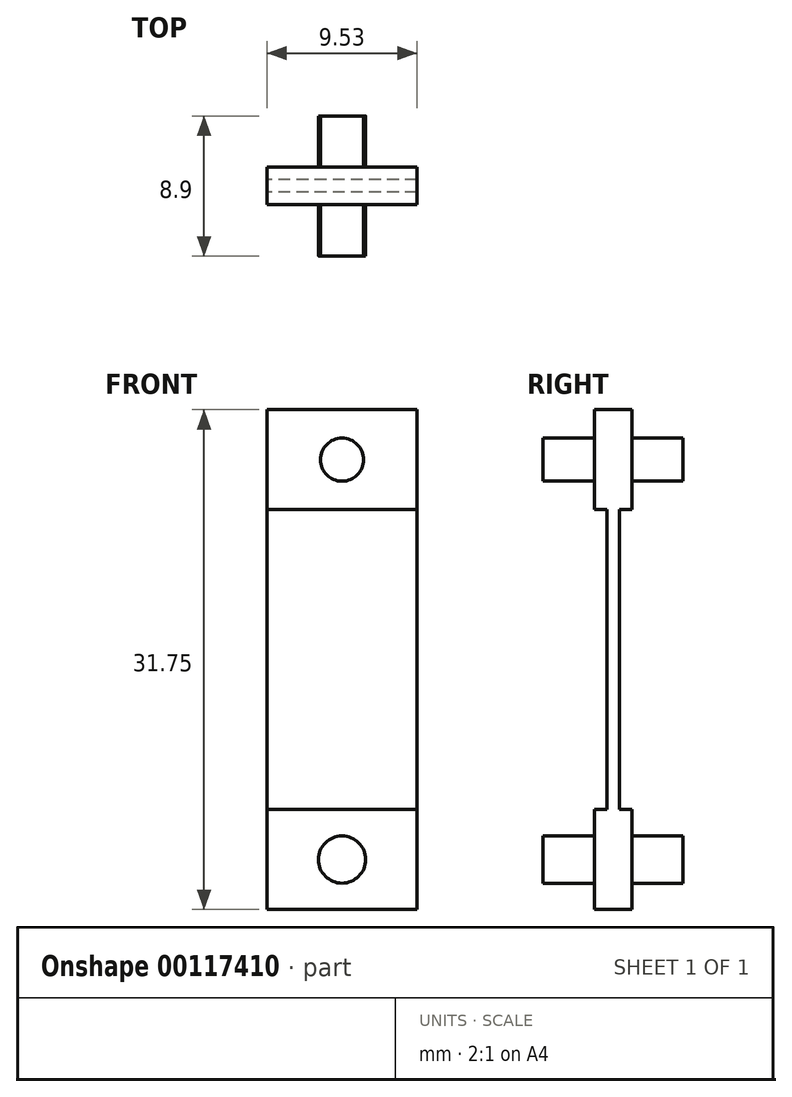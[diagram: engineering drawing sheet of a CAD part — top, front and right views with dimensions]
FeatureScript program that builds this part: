
annotation { "Feature Type Name" : "Feature", "Feature Type Description" : "" }
export const myFeature = defineFeature(function(context is Context, id is Id, definition is map)
    precondition{}
    {
        {
            var Q0;
            Q0=qCreatedBy(makeId("Front.planeOp"),FACE);
            var sketch = newSketch(context, id + "F0", { "sketchPlane" : qUnion([Q0])});
            skLineSegment(sketch, "E0.bottom", {"start": v(-30, 47.14) * mm, "end": v(-20.47, 47.14) * mm});
            skLineSegment(sketch, "E0.top", {"start": v(-30, 15.39) * mm, "end": v(-20.47, 15.39) * mm});
            skLineSegment(sketch, "E0.left", {"start": v(-30, 47.14) * mm, "end": v(-30, 15.39) * mm});
            skLineSegment(sketch, "E0.right", {"start": v(-20.47, 47.14) * mm, "end": v(-20.47, 15.39) * mm});
            skLineSegment(sketch, "E1", {"start": v(-20.47, 40.79) * mm, "end": v(-30, 40.79) * mm});
            skLineSegment(sketch, "E2", {"start": v(-20.47, 21.74) * mm, "end": v(-30, 21.74) * mm});
            skCircle(sketch, "E3", {"center": v(-25.24, 43.96) * mm, "radius": 1.37 * mm});
            skCircle(sketch, "E4", {"center": v(-25.24, 18.56) * mm, "radius": 1.5 * mm});
            skSolve(sketch);
        }
        {
            var Q0;
            {var subQ0=sQuery(id+"F0.wireOp",EDGE,"E1");Q0=makeQuery(id+"F0.imprint","IMPRINT",FACE,{"disambiguationData":[TD([[makeQuery(id+"F0.imprint","IMPRINT",EDGE,{"derivedFrom":subQ0}),1.0]])]});}
            extrude(context, id + "F1", {"entities" : qUnion([Q0]), "endBound" : BoundingType.SYMMETRIC, "depth" : 0.8 * mm});
        }
        {
            var Q0;
            {var subQ2=sQuery(id+"F0.wireOp",EDGE,"E0.bottom");Q0=makeQuery(id+"F0.imprint","IMPRINT",FACE,{"disambiguationData":[TD([[makeQuery(id+"F0.imprint","IMPRINT",EDGE,{"derivedFrom":subQ2}),-1.0]])]});}
            var Q1;
            {var subQ2=sQuery(id+"F0.wireOp",EDGE,"E0.top");Q1=makeQuery(id+"F0.imprint","IMPRINT",FACE,{"disambiguationData":[TD([[makeQuery(id+"F0.imprint","IMPRINT",EDGE,{"derivedFrom":subQ2}),1.0]])]});}
            extrude(context, id + "F2", {"entities" : qUnion([Q0, Q1]), "operationType" : NewBodyOperationType.ADD, "endBound" : BoundingType.SYMMETRIC, "depth" : 2.38 * mm});
        }
        {
            var Q0;
            Q0=makeQuery(id+"F0.imprint","IMPRINT",FACE,{"disambiguationData":[TD([[makeQuery(id+"F0.imprint","IMPRINT",EDGE,{"derivedFrom":sQuery(id+"F0.wireOp",EDGE,"E3")}),1.0]])]});
            var Q1;
            Q1=makeQuery(id+"F0.imprint","IMPRINT",FACE,{"disambiguationData":[TD([[makeQuery(id+"F0.imprint","IMPRINT",EDGE,{"derivedFrom":sQuery(id+"F0.wireOp",EDGE,"E4")}),1.0]])]});
            extrude(context, id + "F3", {"entities" : qUnion([Q0, Q1]), "operationType" : NewBodyOperationType.ADD, "endBound" : BoundingType.SYMMETRIC, "depth" : 8.9 * mm});
        }
    });
